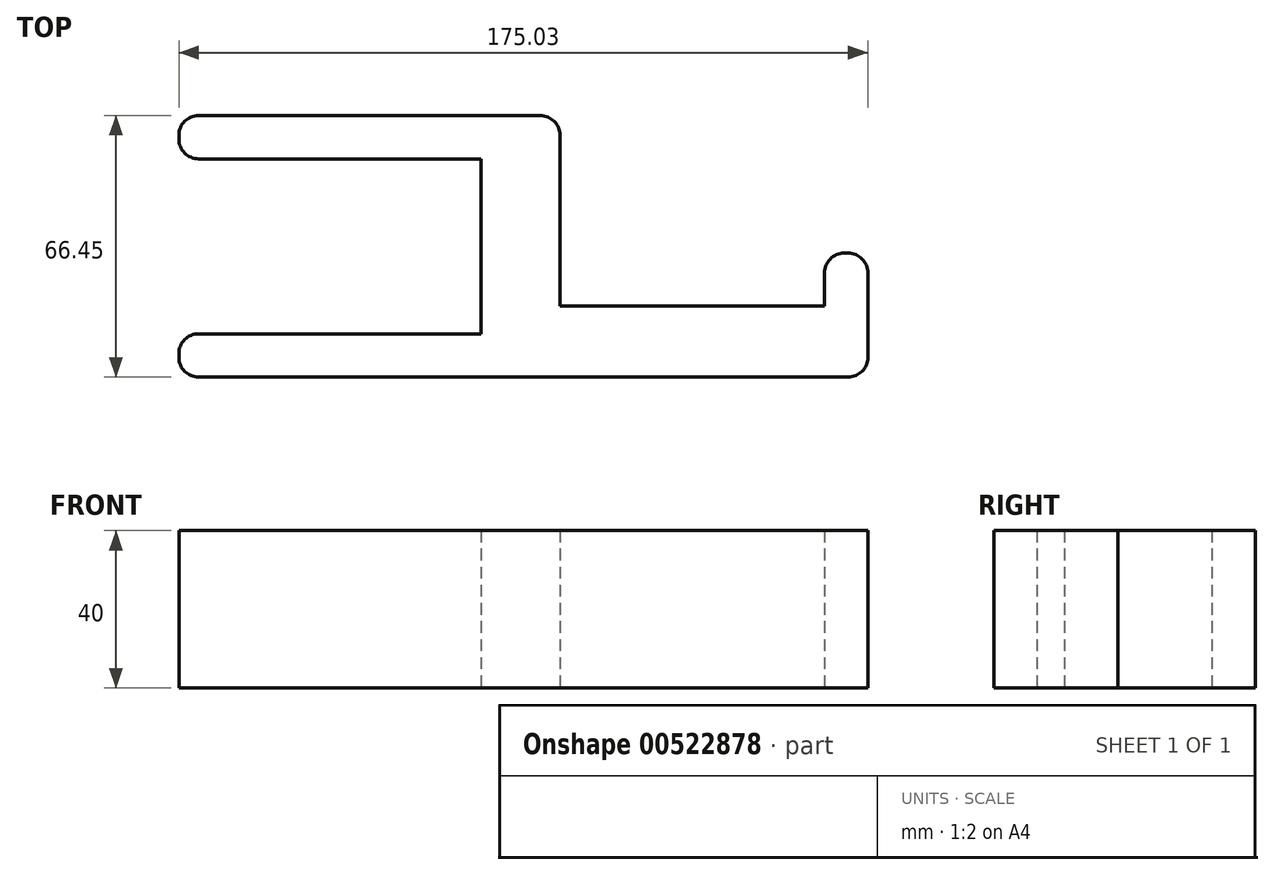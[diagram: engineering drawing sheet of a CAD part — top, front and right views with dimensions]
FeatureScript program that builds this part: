
annotation { "Feature Type Name" : "Feature", "Feature Type Description" : "" }
export const myFeature = defineFeature(function(context is Context, id is Id, definition is map)
    precondition{}
    {
        {
            var Q0;
            Q0=qCreatedBy(makeId("Top.planeOp"),FACE);
            var sketch = newSketch(context, id + "F0", { "sketchPlane" : qUnion([Q0])});
            skLineSegment(sketch, "E0", {"start": v(-88.2, 38.55) * mm, "end": v(-88.2, 27.55) * mm});
            skLineSegment(sketch, "E1", {"start": v(-88.2, 27.55) * mm, "end": v(-11.4, 27.55) * mm});
            skLineSegment(sketch, "E2", {"start": v(-11.4, 27.55) * mm, "end": v(-11.4, -16.9) * mm});
            skLineSegment(sketch, "E3", {"start": v(-11.4, -16.9) * mm, "end": v(-88.2, -16.9) * mm});
            skLineSegment(sketch, "E4", {"start": v(-88.2, -16.9) * mm, "end": v(-88.2, -27.9) * mm});
            skLineSegment(sketch, "E5", {"start": v(-88.2, -27.9) * mm, "end": v(86.83, -27.9) * mm});
            skLineSegment(sketch, "E6", {"start": v(86.83, -27.9) * mm, "end": v(86.83, 3.57) * mm});
            skLineSegment(sketch, "E7", {"start": v(75.83, 3.57) * mm, "end": v(75.83, -9.9) * mm});
            skLineSegment(sketch, "E8", {"start": v(75.83, -9.9) * mm, "end": v(8.6, -9.9) * mm});
            skLineSegment(sketch, "E9", {"start": v(8.6, -9.9) * mm, "end": v(8.6, 38.55) * mm});
            skLineSegment(sketch, "E10", {"start": v(8.6, 38.55) * mm, "end": v(-88.2, 38.55) * mm});
            skLineSegment(sketch, "E11", {"start": v(75.83, 3.57) * mm, "end": v(86.83, 3.57) * mm});
            skSolve(sketch);
        }
        {
            var Q0;
            Q0=makeQuery(id+"F0.imprint","IMPRINT",FACE,{"disambiguationData":[TD([[makeQuery(id+"F0.imprint","IMPRINT",EDGE,{"derivedFrom":sQuery(id+"F0.wireOp",EDGE,"E0")}),1.0]])]});
            extrude(context, id + "F1", {"entities" : qUnion([Q0]), "depth" : 40 * mm, "offsetDistance" : 25 * mm});
        }
        {
            var Q0;
            Q0=makeQuery(id+"F1.opExtrude","SWEPT_EDGE",EDGE,{"disambiguationData":[OSD([sQuery(id+"F0.wireOp",EDGE,"E9"),sQuery(id+"F0.wireOp",EDGE,"E10")])]});
            var Q1;
            Q1=makeQuery(id+"F1.opExtrude","SWEPT_EDGE",EDGE,{"disambiguationData":[OSD([sQuery(id+"F0.wireOp",EDGE,"E5"),sQuery(id+"F0.wireOp",EDGE,"E6")])]});
            var Q2;
            Q2=makeQuery(id+"F1.opExtrude","SWEPT_EDGE",EDGE,{"disambiguationData":[OSD([sQuery(id+"F0.wireOp",EDGE,"E4"),sQuery(id+"F0.wireOp",EDGE,"E5")])]});
            var Q3;
            Q3=makeQuery(id+"F1.opExtrude","SWEPT_EDGE",EDGE,{"disambiguationData":[OSD([sQuery(id+"F0.wireOp",EDGE,"E3"),sQuery(id+"F0.wireOp",EDGE,"E4")])]});
            var Q4;
            Q4=makeQuery(id+"F1.opExtrude","SWEPT_EDGE",EDGE,{"disambiguationData":[OSD([sQuery(id+"F0.wireOp",EDGE,"E0"),sQuery(id+"F0.wireOp",EDGE,"E1")])]});
            var Q5;
            Q5=makeQuery(id+"F1.opExtrude","SWEPT_EDGE",EDGE,{"disambiguationData":[OSD([sQuery(id+"F0.wireOp",EDGE,"E0"),sQuery(id+"F0.wireOp",EDGE,"E10")])]});
            var Q6;
            Q6=makeQuery(id+"F1.opExtrude","SWEPT_EDGE",EDGE,{"disambiguationData":[OSD([sQuery(id+"F0.wireOp",EDGE,"E6"),sQuery(id+"F0.wireOp",EDGE,"E11")])]});
            var Q7;
            Q7=makeQuery(id+"F1.opExtrude","SWEPT_EDGE",EDGE,{"disambiguationData":[OSD([sQuery(id+"F0.wireOp",EDGE,"E7"),sQuery(id+"F0.wireOp",EDGE,"E11")])]});
            fillet(context, id + "F2", {"entities" : qUnion([Q0, Q1, Q2, Q3, Q4, Q5, Q6, Q7]), "radius" : 5 * mm, "tangentPropagation" : true, "allowEdgeOverflow" : false});
        }
    });
